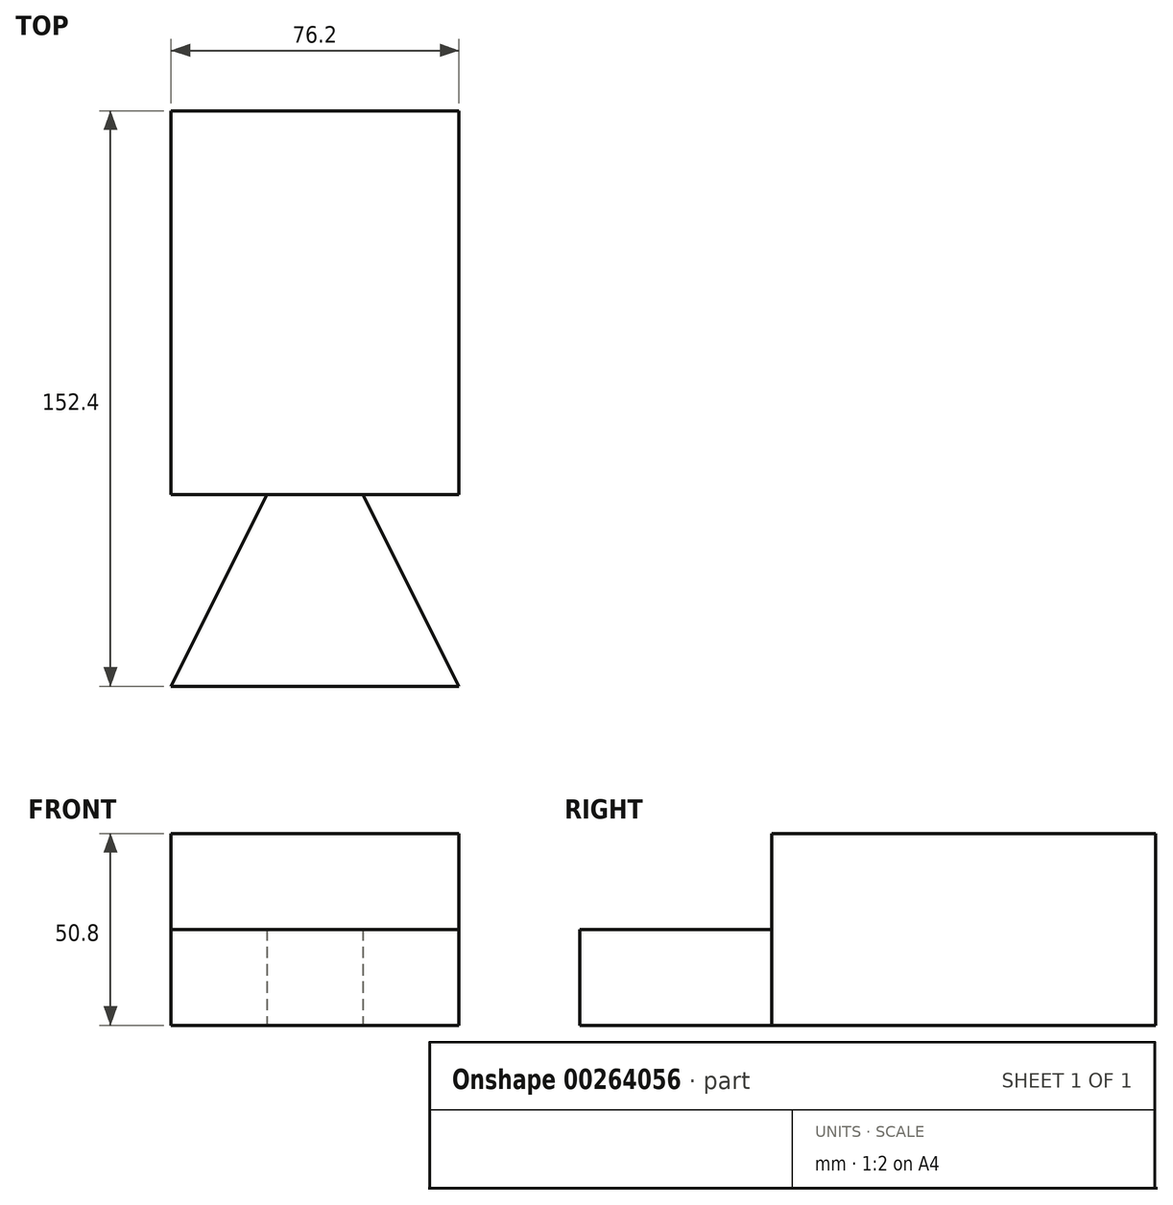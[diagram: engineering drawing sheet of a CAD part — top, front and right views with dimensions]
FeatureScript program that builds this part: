
annotation { "Feature Type Name" : "Feature", "Feature Type Description" : "" }
export const myFeature = defineFeature(function(context is Context, id is Id, definition is map)
    precondition{}
    {
        {
            var Q0;
            Q0=qCreatedBy(makeId("Top.planeOp"),FACE);
            var sketch = newSketch(context, id + "F0", { "sketchPlane" : qUnion([Q0])});
            skLineSegment(sketch, "E0", {"start": v(-35.4, 78.44) * mm, "end": v(-35.4, -23.16) * mm});
            skLineSegment(sketch, "E1", {"start": v(-35.4, 78.44) * mm, "end": v(40.8, 78.44) * mm});
            skLineSegment(sketch, "E2", {"start": v(40.8, 78.44) * mm, "end": v(40.8, -23.16) * mm});
            skLineSegment(sketch, "E3", {"start": v(-35.4, -23.16) * mm, "end": v(-10, -23.16) * mm});
            skLineSegment(sketch, "E4", {"start": v(40.8, -23.16) * mm, "end": v(15.4, -23.16) * mm});
            skLineSegment(sketch, "E5", {"start": v(-10, -23.16) * mm, "end": v(-35.4, -73.96) * mm});
            skLineSegment(sketch, "E6", {"start": v(-35.4, -73.96) * mm, "end": v(40.8, -73.96) * mm});
            skLineSegment(sketch, "E7", {"start": v(15.4, -23.16) * mm, "end": v(40.8, -73.96) * mm});
            skLineSegment(sketch, "E8", {"start": v(-10, -23.16) * mm, "end": v(15.4, -23.16) * mm});
            skSolve(sketch);
        }
        {
            var Q0;
            Q0=makeQuery(id+"F0.imprint","IMPRINT",FACE,{"disambiguationData":[TD([[makeQuery(id+"F0.imprint","IMPRINT",EDGE,{"derivedFrom":sQuery(id+"F0.wireOp",EDGE,"E5")}),1.0]])]});
            var Q1;
            Q1=makeQuery(id+"F0.imprint","IMPRINT",FACE,{"disambiguationData":[TD([[makeQuery(id+"F0.imprint","IMPRINT",EDGE,{"derivedFrom":sQuery(id+"F0.wireOp",EDGE,"E0")}),1.0]])]});
            extrude(context, id + "F1", {"entities" : qUnion([Q0, Q1]), "depth" : 25.4 * mm});
        }
        {
            var Q0;
            Q0=makeQuery(id+"F1.opExtrude","CAP_FACE",FACE,{"disambiguationData":[OSD([sQuery(id+"F0.wireOp",EDGE,"E0"),sQuery(id+"F0.wireOp",EDGE,"E1"),sQuery(id+"F0.wireOp",EDGE,"E2"),sQuery(id+"F0.wireOp",EDGE,"E3"),sQuery(id+"F0.wireOp",EDGE,"E4"),sQuery(id+"F0.wireOp",EDGE,"E5"),sQuery(id+"F0.wireOp",EDGE,"E6"),sQuery(id+"F0.wireOp",EDGE,"E7")])],"isStart":false});
            var sketch = newSketch(context, id + "F2", { "sketchPlane" : qUnion([Q0])});
            skLineSegment(sketch, "E9.bottom", {"start": v(40.8, 78.44) * mm, "end": v(-35.4, 78.44) * mm});
            skLineSegment(sketch, "E9.top", {"start": v(40.8, -23.16) * mm, "end": v(-35.4, -23.16) * mm});
            skLineSegment(sketch, "E9.left", {"start": v(40.8, 78.44) * mm, "end": v(40.8, -23.16) * mm});
            skLineSegment(sketch, "E9.right", {"start": v(-35.4, 78.44) * mm, "end": v(-35.4, -23.16) * mm});
            skSolve(sketch);
        }
        {
            var Q0;
            Q0=makeQuery(id+"F2.imprint","IMPRINT",FACE,{"disambiguationData":[TD([[makeQuery(id+"F2.imprint","IMPRINT",EDGE,{"derivedFrom":sQuery(id+"F2.wireOp",EDGE,"E9.bottom")}),-1.0]])]});
            extrude(context, id + "F3", {"entities" : qUnion([Q0]), "operationType" : NewBodyOperationType.ADD, "depth" : 25.4 * mm});
        }
    });
